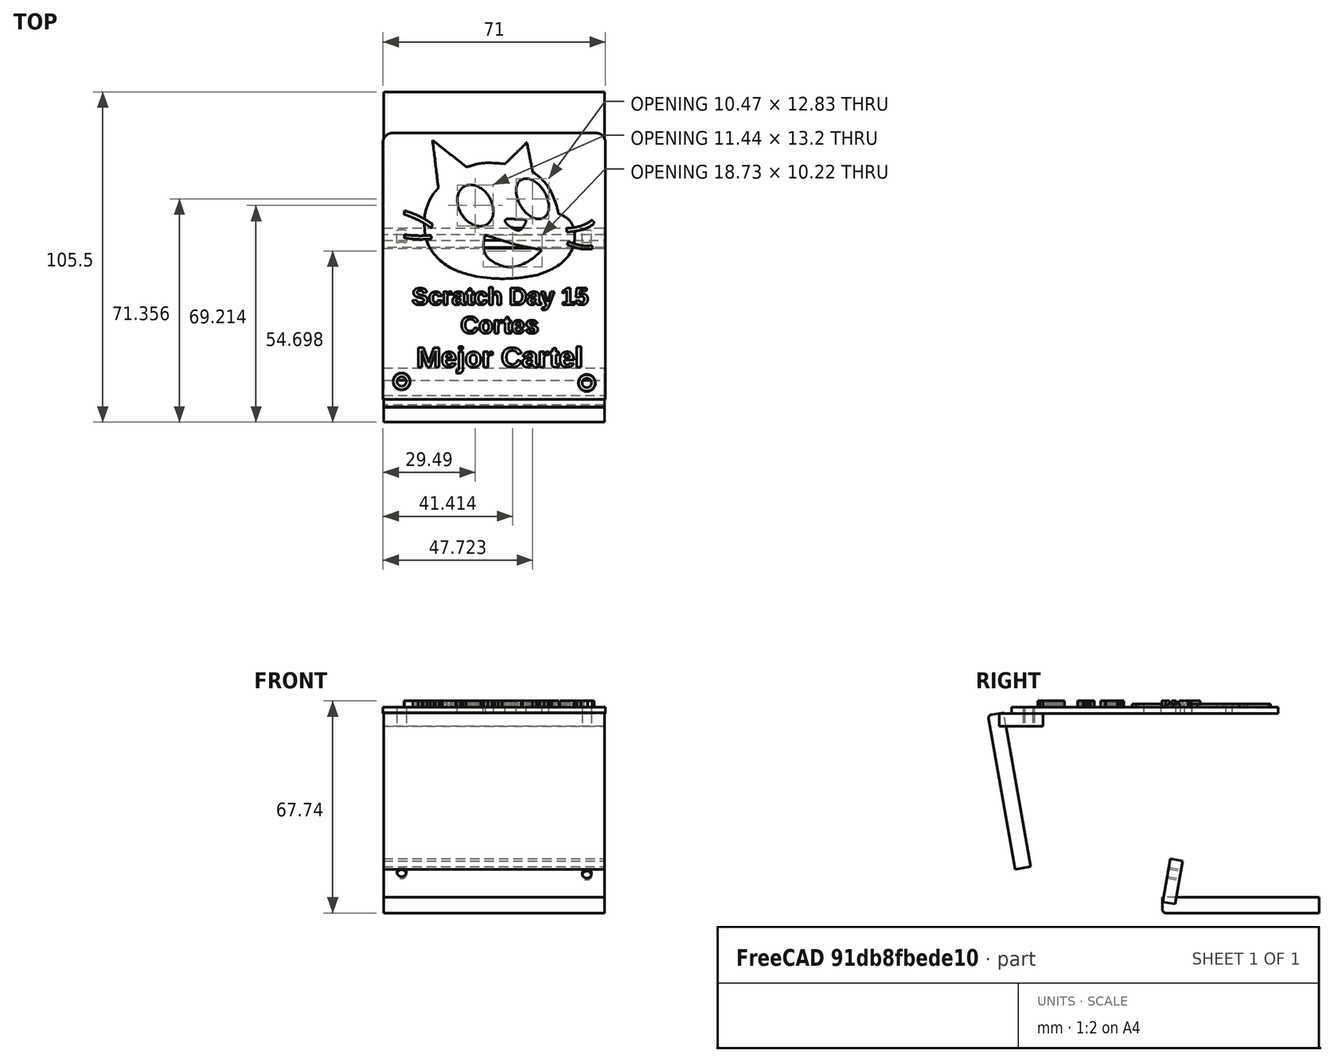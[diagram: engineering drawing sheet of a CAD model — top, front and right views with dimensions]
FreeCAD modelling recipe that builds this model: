
FCSTD DOCUMENT  (FreeCAD 0.14R3702 (Git))
Label: Trofeo Scratch
License: CC-BY 3.0
LicenseURL: http://creativecommons.org/licenses/by/3.0/
objects: Part::Feature×13, Part::Extrusion×12, Part::MultiFuse×4, Part::Cut×4, Part::Box×3, Part::Part2DObjectPython×3, Part::Fillet×2
note: 41 computed .brp shape members not serialized (recipe doc carries the construction recipe); baked Part::Feature solids carry a one-line shape summary decoded from their .brp

FEATURE [Part::Feature] path
  shape: bbox 48.25 x 45.35 x 2e-07 mm, 0 faces, 0 solids (baked)
FEATURE [Part::Feature] path3973_
  shape: bbox 12.16 x 13.86 x 2e-07 mm, 0 faces, 0 solids (baked)
FEATURE [Part::Feature] path3981_
  shape: bbox 11.18 x 13.57 x 2e-07 mm, 0 faces, 0 solids (baked)
FEATURE [Part::Feature] path4045_
  shape: bbox 19.5 x 11.04 x 2e-07 mm, 0 faces, 0 solids (baked)
FEATURE [Part::Feature] path3993_1_
  shape: bbox 6.742 x 3.801 x 2e-07 mm, 1 faces, 0 solids (baked)
FEATURE [Part::Feature] path001
  shape: bbox 9.018 x 5.518 x 2e-07 mm, 0 faces, 0 solids (baked)
FEATURE [Part::Feature] path002
  shape: bbox 8.682 x 1.641 x 2e-07 mm, 0 faces, 0 solids (baked)
FEATURE [Part::Feature] path003
  shape: bbox 8.914 x 3.82 x 2e-07 mm, 0 faces, 0 solids (baked)
FEATURE [Part::Feature] path004
  shape: bbox 7.988 x 2.613 x 2e-07 mm, 0 faces, 0 solids (baked)
FEATURE [Part::Box] Box  label="Cubo"
  Height = 2
  Length = 71
  Placement = pos=(-37.7424,-57.9426,-0.991511) rot=(0,0,1;0rad)
  Width = 85
FEATURE [Part::Part2DObjectPython] ShapeString002  # Draft 2D object (typed FeaturePython)
  FontFile = <path>
  Placement = pos=(-13.454,-24.3602,0) rot=(0,0,1;0rad)
  Size = 6
  String = Scratch Day 15
  Tracking = 0
FEATURE [Part::Extrusion] Extrude024
  Base = -> ShapeString002
  Dir = (0,0,2)
  Placement = pos=(-15.006,-3.48125,0.999991) rot=(0,0,1;0rad)
  Solid = true
FEATURE [Part::Part2DObjectPython] ShapeString004  # Draft 2D object (typed FeaturePython)
  FontFile = <path>
  Placement = pos=(-13.454,-24.3602,0) rot=(0,0,1;0rad)
  Size = 7
  String = Mejor Cartel
  Tracking = 0
FEATURE [Part::Extrusion] Extrude026  label="TextoEstruido"
  Base = -> ShapeString004
  Dir = (0,0,2)
  Placement = pos=(-13.6044,-23.3916,0.999858) rot=(0,0,1;0rad)
  Solid = true
FEATURE [Part::Extrusion] Extrude028
  Base = -> path004
  Dir = (0,0,3)
  Solid = true
FEATURE [Part::Extrusion] Extrude029
  Base = -> path001
  Dir = (0,0,3)
  Solid = true
FEATURE [Part::Extrusion] Extrude030
  Base = -> path002
  Dir = (0,0,3)
  Solid = true
FEATURE [Part::Extrusion] Extrude032
  Base = -> path3973_
  Dir = (0,0,6)
  Solid = true
FEATURE [Part::Extrusion] Extrude033
  Base = -> path003
  Dir = (0,0,3)
  Solid = true
FEATURE [Part::Extrusion] Extrude034
  Base = -> path3993_1_
  Dir = (0,0,6)
  Solid = true
FEATURE [Part::Extrusion] Extrude035
  Base = -> path4045_
  Dir = (0,0,6)
  Solid = true
FEATURE [Part::Extrusion] Extrude036
  Base = -> path3981_
  Dir = (0,0,6)
  Solid = true
FEATURE [Part::Extrusion] Extrude037
  Base = -> path
  Dir = (0,0,2)
  Solid = true
FEATURE [Part::Part2DObjectPython] ShapeString005  # Draft 2D object (typed FeaturePython)
  FontFile = <path>
  Placement = pos=(-13.454,-24.3602,0) rot=(0,0,1;0rad)
  Size = 6
  String = Cortes
  Tracking = 0
FEATURE [Part::Extrusion] Extrude038
  Base = -> ShapeString005
  Dir = (0,0,2)
  Placement = pos=(0.501886,-12.5972,0.999962) rot=(0,0,1;0rad)
  Solid = true
FEATURE [Part::MultiFuse] Fusion004
  Placement = pos=(0,0,-1) rot=(0,0,1;0rad)
  Shapes = -> [Extrude034,Extrude035,Extrude032,Extrude036]
FEATURE [Part::Fillet] Fillet
  Base = -> Box
  Edges = 2 edges r=3: [Edge3,Edge7]
FEATURE [Part::MultiFuse] Fusion005
  Shapes = -> [Fillet,Extrude033,Extrude028,Extrude029,Extrude030,Extrude037,Extrude038,Extrude026,Extrude024]
FEATURE [Part::Cut] Cut  label="Frontal"
  Base = -> Fusion005
  Tool = -> Fusion004
FEATURE [Part::Feature] Part__Feature  label="Chamfer005"
  Placement = pos=(27.2337,-52.621,20.2591) rot=(0,0,1;0rad)
  shape: bbox 6.35 x 6.35 x 2.4 mm, 29 faces (baked)
FEATURE [Part::Feature] Part__Feature001  label="Chamfer002"
  Placement = pos=(-31.7737,-52.284,20.2591) rot=(0,0,1;0rad)
  shape: bbox 6.35 x 6.35 x 2.4 mm, 29 faces (baked)
FEATURE [Part::Feature] Part__Feature002  label="Chamfer004"
  Placement = pos=(27.3367,-52.7409,28.9364) rot=(0,0,1;0rad)
  shape: bbox 5.5 x 5.5 x 15 mm, 16 faces (baked)
FEATURE [Part::Feature] Part__Feature003  label="Chamfer003"
  Placement = pos=(-31.7766,-52.2852,28.9365) rot=(0,0,1;0rad)
  shape: bbox 5.5 x 5.5 x 15 mm, 16 faces (baked)
FEATURE [Part::MultiFuse] Fusion  label="tornilleria futaba"
  Placement = pos=(0,0,-28) rot=(0,0,1;0rad)
  Shapes = -> [Part__Feature003,Part__Feature002,Part__Feature001,Part__Feature]
FEATURE [Part::Box] Box001  label="Cubo001"
  Height = 4
  Length = 70.5
  Placement = pos=(-37.5258,-61.9669,-5.08684) rot=(0,0,1;0rad)
  Width = 14
FEATURE [Part::Box] Box002  label="Cubo002"
  Height = 50
  Length = 70.5
  Placement = pos=(-37.5646,-56.778,-50.8302) rot=(1,0,0;0.174533rad)
  Width = 5
FEATURE [Part::MultiFuse] Fusion006
  Shapes = -> [Box001,Box002]
FEATURE [Part::Fillet] Fillet001
  Base = -> Fusion006
  Edges = 1 edges r=1: [Edge28]
FEATURE [Part::Cut] Cut001
  Base = -> Cut
  Tool = -> Fusion
FEATURE [Part::Cut] Cut002
  Base = -> Fillet001
  Tool = -> Fusion
FEATURE [Part::Cut] Cut003
  Base = -> Fillet001
  Placement = pos=(0,0,0) rot=(1,0,0;1.39626rad)
  Tool = -> Fusion
note: 3 file-system paths scrubbed to <path> (originals preserved in the JSON sidecar)
